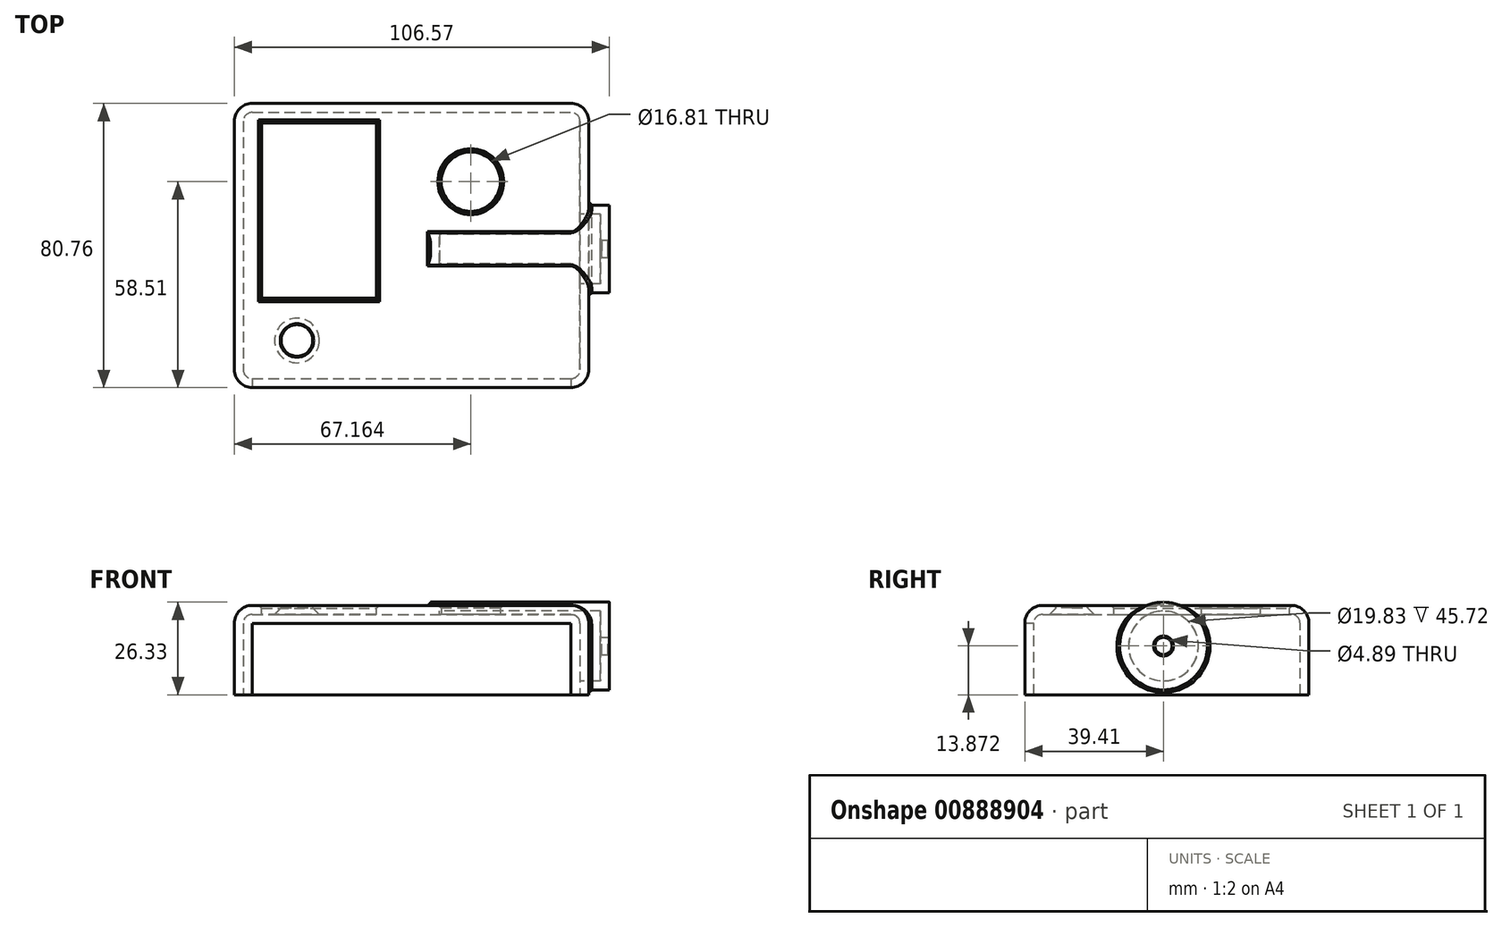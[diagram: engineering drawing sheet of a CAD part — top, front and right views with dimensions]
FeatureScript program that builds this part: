
annotation { "Feature Type Name" : "Feature", "Feature Type Description" : "" }
export const myFeature = defineFeature(function(context is Context, id is Id, definition is map)
    precondition{}
    {
        {
            var Q0;
            Q0=qCreatedBy(makeId("Top.planeOp"),FACE);
            var sketch = newSketch(context, id + "F0", { "sketchPlane" : qUnion([Q0])});
            skLineSegment(sketch, "E0.bottom", {"start": v(-55.77, 41.35) * mm, "end": v(44.97, 41.35) * mm});
            skLineSegment(sketch, "E0.top", {"start": v(-55.77, -39.41) * mm, "end": v(44.97, -39.41) * mm});
            skLineSegment(sketch, "E0.left", {"start": v(-55.77, 41.35) * mm, "end": v(-55.77, -39.41) * mm});
            skLineSegment(sketch, "E0.right", {"start": v(44.97, 41.35) * mm, "end": v(44.97, -39.41) * mm});
            skSolve(sketch);
        }
        {
            var Q0;
            Q0=makeQuery(id+"F0.imprint","IMPRINT",FACE,{"disambiguationData":[TD([[makeQuery(id+"F0.imprint","IMPRINT",EDGE,{"derivedFrom":sQuery(id+"F0.wireOp",EDGE,"E0.bottom")}),-1.0]])]});
            extrude(context, id + "F1", {"entities" : qUnion([Q0]), "depth" : 25.4 * mm, "offsetDistance" : 25.4 * mm});
        }
        {
            var Q0;
            Q0=qCreatedBy(makeId("Right.planeOp"),FACE);
            var sketch = newSketch(context, id + "F2", { "sketchPlane" : qUnion([Q0])});
            skCircle(sketch, "E1", {"center": v(0, 13.87) * mm, "radius": 12.45 * mm});
            skSolve(sketch);
        }
        {
            var Q0;
            Q0=makeQuery(id+"F2.imprint","IMPRINT",FACE,{"disambiguationData":[TD([[makeQuery(id+"F2.imprint","IMPRINT",EDGE,{"derivedFrom":sQuery(id+"F2.wireOp",EDGE,"E1")}),1.0]])]});
            extrude(context, id + "F3", {"entities" : qUnion([Q0]), "operationType" : NewBodyOperationType.ADD, "depth" : 50.8 * mm, "offsetDistance" : 25.4 * mm});
        }
        {
            var Q0;
            {var subQ0=sQuery(id+"F0.wireOp",EDGE,"E0.bottom");var subQ1=sQuery(id+"F0.wireOp",EDGE,"E0.right");Q0=makeQuery(id+"F3.boolean.opBoolean","SPLIT",EDGE,{"disambiguationData":[TD([makeQuery(id+"F1.opExtrude","SWEPT_FACE",FACE,{"disambiguationData":[OSD([subQ0])]})])],"derivedFrom":makeQuery(id+"F1.opExtrude","CAP_EDGE",EDGE,{"disambiguationData":[OSD([subQ1])],"isStart":false})});}
            var Q1;
            Q1=makeQuery(id+"F1.opExtrude","CAP_EDGE",EDGE,{"disambiguationData":[OSD([sQuery(id+"F0.wireOp",EDGE,"E0.top")])],"isStart":false});
            var Q2;
            Q2=makeQuery(id+"F1.opExtrude","SWEPT_EDGE",EDGE,{"disambiguationData":[OSD([sQuery(id+"F0.wireOp",EDGE,"E0.bottom"),sQuery(id+"F0.wireOp",EDGE,"E0.right")])]});
            var Q3;
            Q3=makeQuery(id+"F1.opExtrude","SWEPT_EDGE",EDGE,{"disambiguationData":[OSD([sQuery(id+"F0.wireOp",EDGE,"E0.top"),sQuery(id+"F0.wireOp",EDGE,"E0.right")])]});
            var Q4;
            {var subQ0=sQuery(id+"F0.wireOp",EDGE,"E0.right");var subQ1=sQuery(id+"F0.wireOp",EDGE,"E0.top");Q4=makeQuery(id+"F3.boolean.opBoolean","SPLIT",EDGE,{"disambiguationData":[TD([makeQuery(id+"F1.opExtrude","SWEPT_FACE",FACE,{"disambiguationData":[OSD([subQ1])]})])],"derivedFrom":makeQuery(id+"F1.opExtrude","CAP_EDGE",EDGE,{"disambiguationData":[OSD([subQ0])],"isStart":false})});}
            fillet(context, id + "F4", {"entities" : qUnion([Q0, Q1, Q2, Q3, Q4]), "radius" : 5.08 * mm, "tangentPropagation" : true, "allowEdgeOverflow" : false});
        }
        {
            var Q0;
            {var subQ0=sQuery(id+"F0.wireOp",EDGE,"E0.bottom");var subQ1=sQuery(id+"F0.wireOp",EDGE,"E0.right");Q0=makeQuery(id+"F4.opFillet","BLEND_EDGE",EDGE,{"blendedFrom":[makeQuery(id+"F1.opExtrude","SWEPT_EDGE",EDGE,{"disambiguationData":[OSD([subQ0,subQ1])]}),makeQuery(id+"F3.boolean.opBoolean","SPLIT",EDGE,{"disambiguationData":[TD([makeQuery(id+"F1.opExtrude","SWEPT_FACE",FACE,{"disambiguationData":[OSD([subQ0])]})])],"derivedFrom":makeQuery(id+"F1.opExtrude","CAP_EDGE",EDGE,{"disambiguationData":[OSD([subQ1])],"isStart":false})})],"blendedInto":[]});}
            var Q1;
            Q1=makeQuery(id+"F1.opExtrude","SWEPT_EDGE",EDGE,{"disambiguationData":[OSD([sQuery(id+"F0.wireOp",EDGE,"E0.bottom"),sQuery(id+"F0.wireOp",EDGE,"E0.left")])]});
            var Q2;
            Q2=makeQuery(id+"F1.opExtrude","SWEPT_EDGE",EDGE,{"disambiguationData":[OSD([sQuery(id+"F0.wireOp",EDGE,"E0.top"),sQuery(id+"F0.wireOp",EDGE,"E0.left")])]});
            fillet(context, id + "F5", {"entities" : qUnion([Q0, Q1, Q2]), "radius" : 5.08 * mm, "tangentPropagation" : true, "allowEdgeOverflow" : false});
        }
        {
            var Q0;
            Q0=makeQuery(id+"F1.opExtrude","CAP_FACE",FACE,{"disambiguationData":[OSD([sQuery(id+"F0.wireOp",EDGE,"E0.bottom"),sQuery(id+"F0.wireOp",EDGE,"E0.top"),sQuery(id+"F0.wireOp",EDGE,"E0.left"),sQuery(id+"F0.wireOp",EDGE,"E0.right")])],"isStart":true});
            shell(context, id + "F6", {"entities" : qUnion([Q0]), "thickness" : 2.54 * mm});
        }
        {
            var Q0;
            Q0=makeQuery(id+"F1.opExtrude","CAP_FACE",FACE,{"disambiguationData":[OSD([sQuery(id+"F0.wireOp",EDGE,"E0.bottom"),sQuery(id+"F0.wireOp",EDGE,"E0.top"),sQuery(id+"F0.wireOp",EDGE,"E0.left"),sQuery(id+"F0.wireOp",EDGE,"E0.right")])],"isStart":false});
            var sketch = newSketch(context, id + "F7", { "sketchPlane" : qUnion([Q0])});
            skLineSegment(sketch, "E2.bottom", {"start": v(-15.42, -14.05) * mm, "end": v(-48, -14.05) * mm});
            skLineSegment(sketch, "E2.top", {"start": v(-15.42, 35.84) * mm, "end": v(-48, 35.84) * mm});
            skLineSegment(sketch, "E2.left", {"start": v(-15.42, -14.05) * mm, "end": v(-15.42, 35.84) * mm});
            skLineSegment(sketch, "E2.right", {"start": v(-48, -14.05) * mm, "end": v(-48, 35.84) * mm});
            skPoint(sketch, "E2.middle", {"position": v(-31.71, 10.9) * mm});
            skSolve(sketch);
        }
        {
            var Q0;
            Q0 = qSketchRegion(id + "F7", true);
            extrude(context, id + "F8", {"entities" : qUnion([Q0]), "operationType" : NewBodyOperationType.REMOVE, "oppositeDirection" : true, "depth" : 25.4 * mm, "offsetDistance" : 25.4 * mm});
        }
        {
            var Q0;
            Q0=qCreatedBy(makeId("Top.planeOp"),FACE);
            var sketch = newSketch(context, id + "F9", { "sketchPlane" : qUnion([Q0])});
            skCircle(sketch, "E3", {"center": v(11.4, 19.1) * mm, "radius": 8.4 * mm});
            skSolve(sketch);
        }
        {
            var Q0;
            Q0 = qSketchRegion(id + "F9", true);
            extrude(context, id + "F10", {"entities" : qUnion([Q0]), "operationType" : NewBodyOperationType.REMOVE, "depth" : 25.4 * mm, "offsetDistance" : 25.4 * mm});
        }
        {
            var Q0;
            Q0=makeQuery(id+"F1.opExtrude","CAP_FACE",FACE,{"disambiguationData":[OSD([sQuery(id+"F0.wireOp",EDGE,"E0.bottom"),sQuery(id+"F0.wireOp",EDGE,"E0.top"),sQuery(id+"F0.wireOp",EDGE,"E0.left"),sQuery(id+"F0.wireOp",EDGE,"E0.right")])],"isStart":false});
            chamfer(context, id + "F11", {"entities" : qUnion([Q0]), "width" : 0.8 * mm, "tangentPropagation" : true});
        }
        {
            var Q0;
            Q0=makeQuery(id+"F3.opExtrude","CAP_FACE",FACE,{"disambiguationData":[OSD([sQuery(id+"F2.wireOp",EDGE,"E1")])],"isStart":false});
            var sketch = newSketch(context, id + "F12", { "sketchPlane" : qUnion([Q0])});
            skCircle(sketch, "E4", {"center": v(0, 13.87) * mm, "radius": 2.44 * mm});
            skSolve(sketch);
        }
        {
            var Q0;
            Q0 = qSketchRegion(id + "F12", true);
            extrude(context, id + "F13", {"entities" : qUnion([Q0]), "operationType" : NewBodyOperationType.REMOVE, "oppositeDirection" : true, "depth" : 25.4 * mm, "offsetDistance" : 25.4 * mm});
        }
        {
            var Q0;
            Q0=makeQuery(id+"F13.boolean.opBoolean","COPY",FACE,{"derivedFrom":makeQuery(id+"F13.opExtrude","SWEPT_FACE",FACE,{"disambiguationData":[OSD([sQuery(id+"F12.wireOp",EDGE,"E4")])]})});
            chamfer(context, id + "F14", {"entities" : qUnion([Q0]), "width" : 0.4 * mm, "tangentPropagation" : true});
        }
        {
            var Q0;
            Q0=qCreatedBy(makeId("Top.planeOp"),FACE);
            var sketch = newSketch(context, id + "F15", { "sketchPlane" : qUnion([Q0])});
            skCircle(sketch, "E5", {"center": v(-37.99, -26.03) * mm, "radius": 6.06 * mm});
            skSolve(sketch);
        }
        {
            var Q0;
            Q0=makeQuery(id+"F15.imprint","IMPRINT",FACE,{"disambiguationData":[TD([[makeQuery(id+"F15.imprint","IMPRINT",EDGE,{"derivedFrom":sQuery(id+"F15.wireOp",EDGE,"E5")}),1.0]])]});
            extrude(context, id + "F16", {"entities" : qUnion([Q0]), "operationType" : NewBodyOperationType.ADD, "depth" : 25.4 * mm, "offsetDistance" : 25.4 * mm});
        }
        {
            var Q0;
            Q0=makeQuery(id+"F16.opExtrude","CAP_FACE",FACE,{"disambiguationData":[OSD([sQuery(id+"F15.wireOp",EDGE,"E5")])],"isStart":true});
            var sketch = newSketch(context, id + "F17", { "sketchPlane" : qUnion([Q0])});
            skCircle(sketch, "E6", {"center": v(-37.99, 26.03) * mm, "radius": 2.99 * mm});
            skSolve(sketch);
        }
        {
            var Q0;
            Q0=sQuery(id+"F17.wireOp",VERTEX,"E6.center");
            var Q1;
            Q1=makeQuery(id+"F1.opExtrude","SWEPT_BODY",BODY,{"disambiguationData":[OSD([sQuery(id+"F0.wireOp",EDGE,"E0.bottom"),sQuery(id+"F0.wireOp",EDGE,"E0.top"),sQuery(id+"F0.wireOp",EDGE,"E0.left"),sQuery(id+"F0.wireOp",EDGE,"E0.right")])]});
            hole(context, id + "F18", {"style" : HoleStyle.C_SINK, "endStyle" : HoleEndStyle.THROUGH, "holeDiameter" : 6.35 * mm, "cSinkDiameter" : 12.7 * mm, "cSinkAngle" : 90 * degree, "majorDiameter" : 6.35 * mm, "isTappedThrough" : true, "tappedDepth" : 12.7 * mm, "tapClearance" : 3, "locations" : qUnion([Q0]), "scope" : qUnion([Q1])});
        }
        {
            var Q0;
            Q0=makeQuery(id+"F1.opExtrude","CAP_FACE",FACE,{"disambiguationData":[OSD([sQuery(id+"F0.wireOp",EDGE,"E0.bottom"),sQuery(id+"F0.wireOp",EDGE,"E0.top"),sQuery(id+"F0.wireOp",EDGE,"E0.left"),sQuery(id+"F0.wireOp",EDGE,"E0.right")])],"isStart":false});
            chamfer(context, id + "F19", {"entities" : qUnion([Q0]), "width" : 0.4 * mm, "tangentPropagation" : true});
        }
        {
            var Q0;
            Q0=qCreatedBy(makeId("Front.planeOp"),FACE);
            var sketch = newSketch(context, id + "F20", { "sketchPlane" : qUnion([Q0])});
            skCircle(sketch, "E7", {"center": v(8.86, 10.64) * mm, "radius": 8.96 * mm});
            skSolve(sketch);
        }
        {
            var Q0;
            Q0=makeQuery(id+"F1.opExtrude","SWEPT_FACE",FACE,{"disambiguationData":[OSD([sQuery(id+"F0.wireOp",EDGE,"E0.top")])]});
            extrude(context, id + "F21", {"entities" : qUnion([Q0]), "operationType" : NewBodyOperationType.REMOVE, "oppositeDirection" : true, "depth" : 25.4 * mm, "offsetDistance" : 25.4 * mm});
        }
        {
            var Q0;
            Q0 = qSketchRegion(id + "F20", true);
            extrude(context, id + "F22", {"entities" : qUnion([Q0]), "operationType" : NewBodyOperationType.REMOVE, "depth" : 25.4 * mm, "offsetDistance" : 25.4 * mm});
        }
    });
